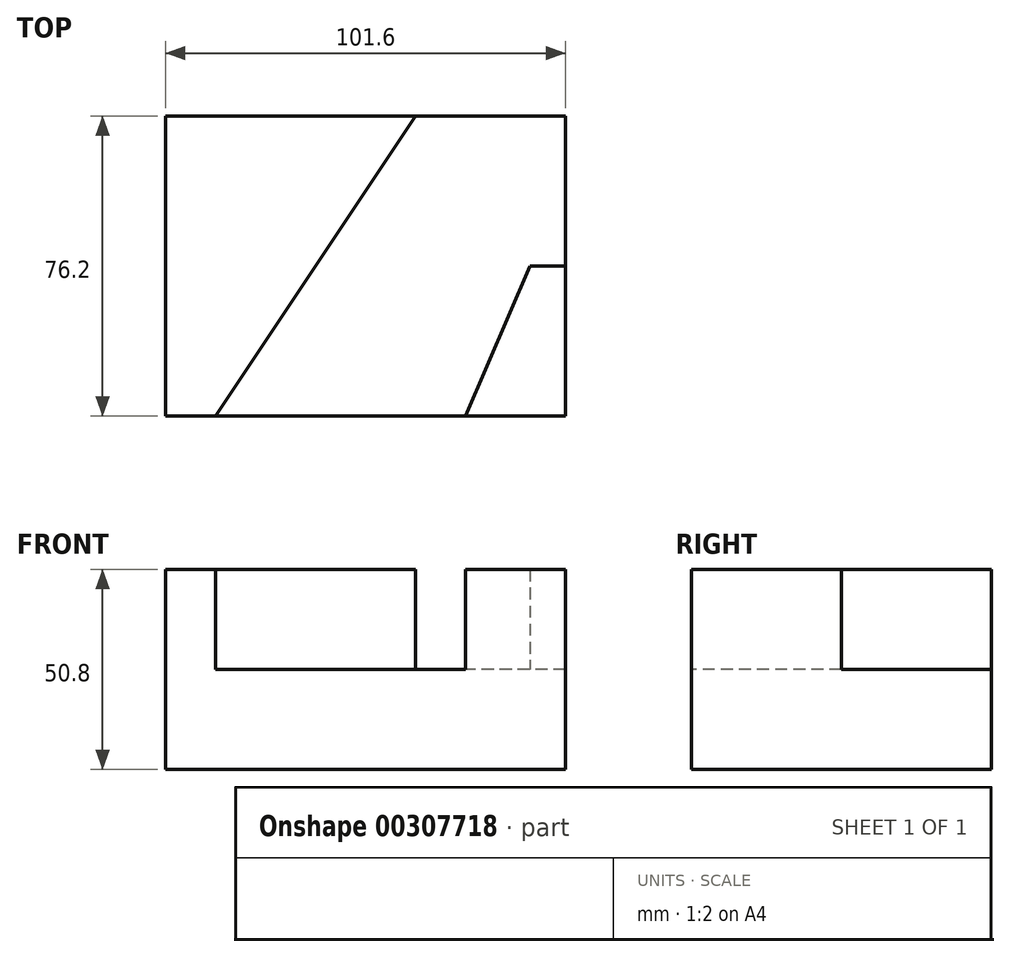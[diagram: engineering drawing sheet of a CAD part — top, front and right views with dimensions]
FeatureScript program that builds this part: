
annotation { "Feature Type Name" : "Feature", "Feature Type Description" : "" }
export const myFeature = defineFeature(function(context is Context, id is Id, definition is map)
    precondition{}
    {
        {
            var Q0;
            Q0=qCreatedBy(makeId("Top.planeOp"),FACE);
            var sketch = newSketch(context, id + "F0", { "sketchPlane" : qUnion([Q0])});
            skLineSegment(sketch, "E0", {"start": v(-53.24, -51.39) * mm, "end": v(48.36, -51.39) * mm});
            skLineSegment(sketch, "E1", {"start": v(48.36, -51.39) * mm, "end": v(48.36, 24.81) * mm});
            skLineSegment(sketch, "E2", {"start": v(48.36, 24.81) * mm, "end": v(-53.24, 24.81) * mm});
            skLineSegment(sketch, "E3", {"start": v(-53.24, 24.81) * mm, "end": v(-53.24, -51.39) * mm});
            skSolve(sketch);
        }
        {
            var Q0;
            Q0=makeQuery(id+"F0.imprint","IMPRINT",FACE,{"disambiguationData":[TD([[makeQuery(id+"F0.imprint","IMPRINT",EDGE,{"derivedFrom":sQuery(id+"F0.wireOp",EDGE,"E0")}),1.0]])]});
            extrude(context, id + "F1", {"entities" : qUnion([Q0]), "depth" : 25.4 * mm});
        }
        {
            var Q0;
            Q0=makeQuery(id+"F1.opExtrude","CAP_FACE",FACE,{"disambiguationData":[OSD([sQuery(id+"F0.wireOp",EDGE,"E0"),sQuery(id+"F0.wireOp",EDGE,"E1"),sQuery(id+"F0.wireOp",EDGE,"E2"),sQuery(id+"F0.wireOp",EDGE,"E3")])],"isStart":false});
            var sketch = newSketch(context, id + "F2", { "sketchPlane" : qUnion([Q0])});
            skLineSegment(sketch, "E4", {"start": v(-53.24, -51.39) * mm, "end": v(-53.24, 24.81) * mm});
            skLineSegment(sketch, "E5", {"start": v(-53.24, 24.81) * mm, "end": v(10.26, 24.81) * mm});
            skLineSegment(sketch, "E6", {"start": v(10.26, 24.81) * mm, "end": v(-40.54, -51.39) * mm});
            skLineSegment(sketch, "E7", {"start": v(-40.54, -51.39) * mm, "end": v(-53.24, -51.39) * mm});
            skSolve(sketch);
        }
        {
            var Q0;
            Q0 = qSketchRegion(id + "F2", true);
            extrude(context, id + "F3", {"entities" : qUnion([Q0]), "operationType" : NewBodyOperationType.ADD, "depth" : 25.4 * mm});
        }
        {
            var Q0;
            Q0=makeQuery(id+"F1.opExtrude","CAP_FACE",FACE,{"disambiguationData":[OSD([sQuery(id+"F0.wireOp",EDGE,"E0"),sQuery(id+"F0.wireOp",EDGE,"E1"),sQuery(id+"F0.wireOp",EDGE,"E2"),sQuery(id+"F0.wireOp",EDGE,"E3")])],"isStart":false});
            var sketch = newSketch(context, id + "F4", { "sketchPlane" : qUnion([Q0])});
            skLineSegment(sketch, "E8", {"start": v(48.36, -51.39) * mm, "end": v(48.36, -13.29) * mm});
            skLineSegment(sketch, "E9", {"start": v(48.36, -13.29) * mm, "end": v(39.34, -13.29) * mm});
            skLineSegment(sketch, "E10", {"start": v(39.34, -13.29) * mm, "end": v(22.96, -51.39) * mm});
            skLineSegment(sketch, "E11", {"start": v(22.96, -51.39) * mm, "end": v(48.36, -51.39) * mm});
            skSolve(sketch);
        }
        {
            var Q0;
            Q0 = qSketchRegion(id + "F4", true);
            extrude(context, id + "F5", {"entities" : qUnion([Q0]), "operationType" : NewBodyOperationType.ADD, "depth" : 25.4 * mm});
        }
    });
